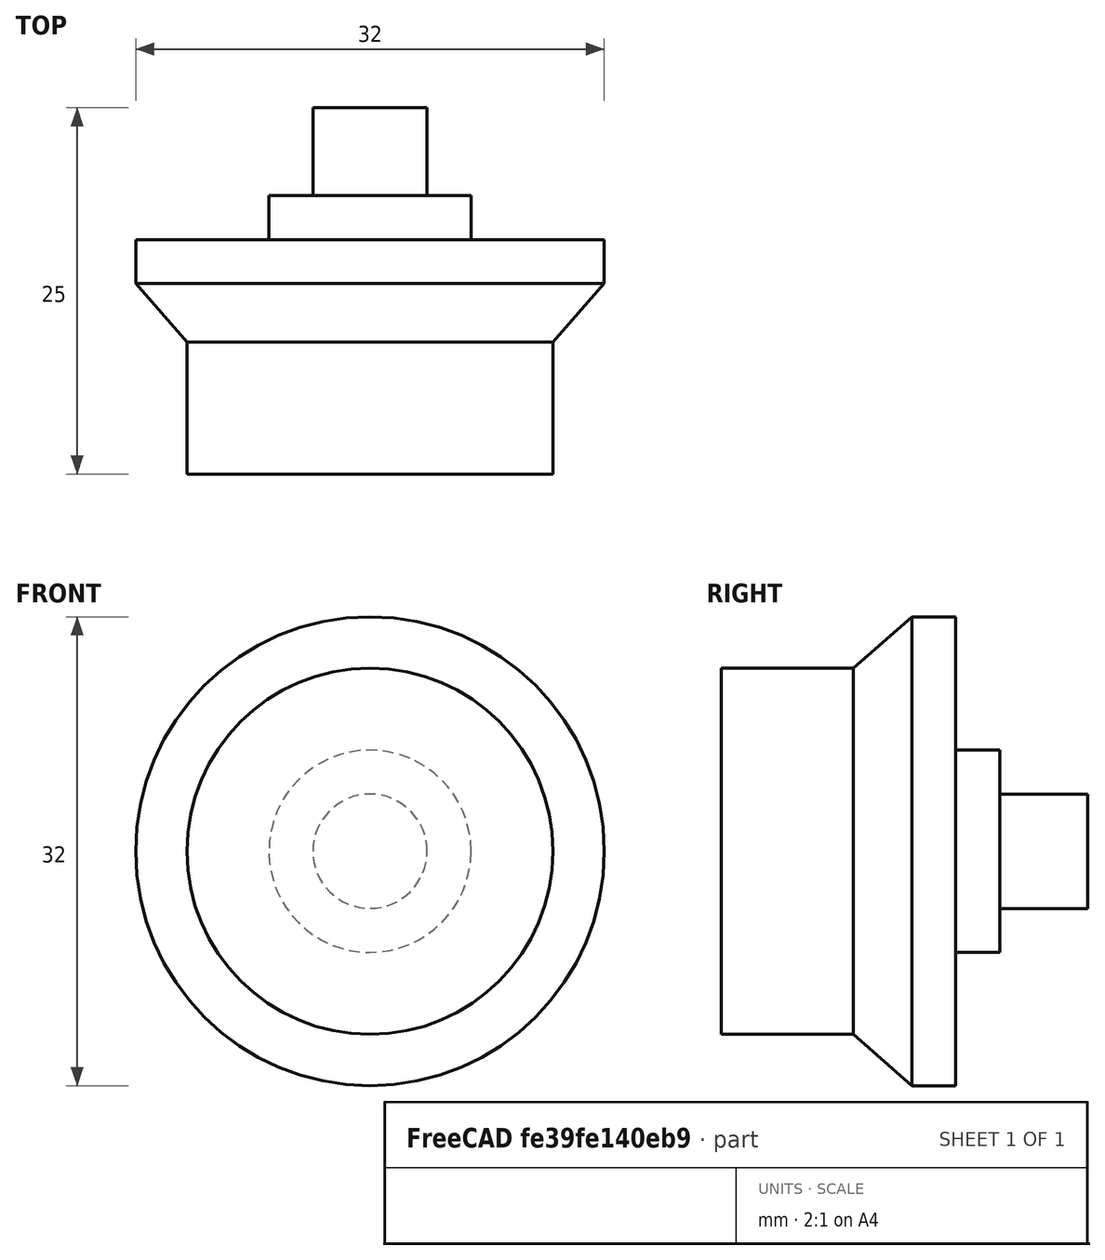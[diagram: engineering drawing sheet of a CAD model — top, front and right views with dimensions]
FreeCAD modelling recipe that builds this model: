
FCSTD DOCUMENT  (FreeCAD 0.14R3702 (Git))
Label: azimuth_axis_pillar
License: CC-BY 3.0
LicenseURL: http://creativecommons.org/licenses/by/3.0/
objects: Sketcher::SketchObject×1, PartDesign::Revolution×1
note: 3 computed .brp shape members not serialized (recipe doc carries the construction recipe); baked Part::Feature solids carry a one-line shape summary decoded from their .brp

FEATURE [Sketcher::SketchObject] Sketch
  sketch-geometry (10):
    g0: LineSegment StartX=0 StartY=25 StartZ=0 EndX=3.9 EndY=25 EndZ=0
    g1: LineSegment StartX=6.9 StartY=19 StartZ=0 EndX=6.9 EndY=16 EndZ=0
    g2: LineSegment StartX=6.9 StartY=16 StartZ=0 EndX=16 EndY=16 EndZ=0
    g3: LineSegment StartX=16 StartY=16 StartZ=0 EndX=16 EndY=13 EndZ=0
    g4: LineSegment StartX=12.5 StartY=9 StartZ=0 EndX=12.5 EndY=0 EndZ=0
    g5: LineSegment StartX=12.5 StartY=0 StartZ=0 EndX=0 EndY=0 EndZ=0
    g6: LineSegment StartX=0 StartY=25 StartZ=0 EndX=0 EndY=0 EndZ=0
    g7: LineSegment StartX=3.9 StartY=25 StartZ=0 EndX=3.9 EndY=19 EndZ=0
    g8: LineSegment StartX=3.9 StartY=19 StartZ=0 EndX=6.9 EndY=19 EndZ=0
    g9: LineSegment StartX=12.5 StartY=9 StartZ=0 EndX=16 EndY=13 EndZ=0
  constraints (29):
    c: Horizontal(g0)
    c: Coincident(g1,g2)
    c: Horizontal(g2)
    c: Coincident(g2,g3)
    c: Vertical(g3)
    c: Vertical(g4)
    c: Coincident(g4,g5)
    c: Horizontal(g5)
    c: Coincident(g6,g0)
    c: Coincident(g6,g5)
    c: Distance(g0) = 3.9
    c: Coincident(g0,g7)
    c: Vertical(g7)
    c: Coincident(g7,g8)
    c: Horizontal(g8)
    c: Vertical(g1)
    c: Coincident(g1,g8)
    c: Distance(g8) = 3
    c: Distance(g7) = 6
    c: DistanceX(g-2,g2) = 16
    c: Vertical(g6)
    c: DistanceX(g5) = -12.5
    c: Coincident(g5,g-1)
    c: DistanceY(g6) = -25
    c: DistanceY(g1) = -3
    c: DistanceY(g3) = -3
    c: Coincident(g9,g4)
    c: Coincident(g9,g3)
    c: DistanceY(g4) = -9
FEATURE [PartDesign::Revolution] Revolution
  Angle = 360
  Axis = (0,1,0)
  Base = (0,0,0)
  ReferenceAxis = -> Sketch [V_Axis]
  Reversed = true
  Sketch = -> Sketch
